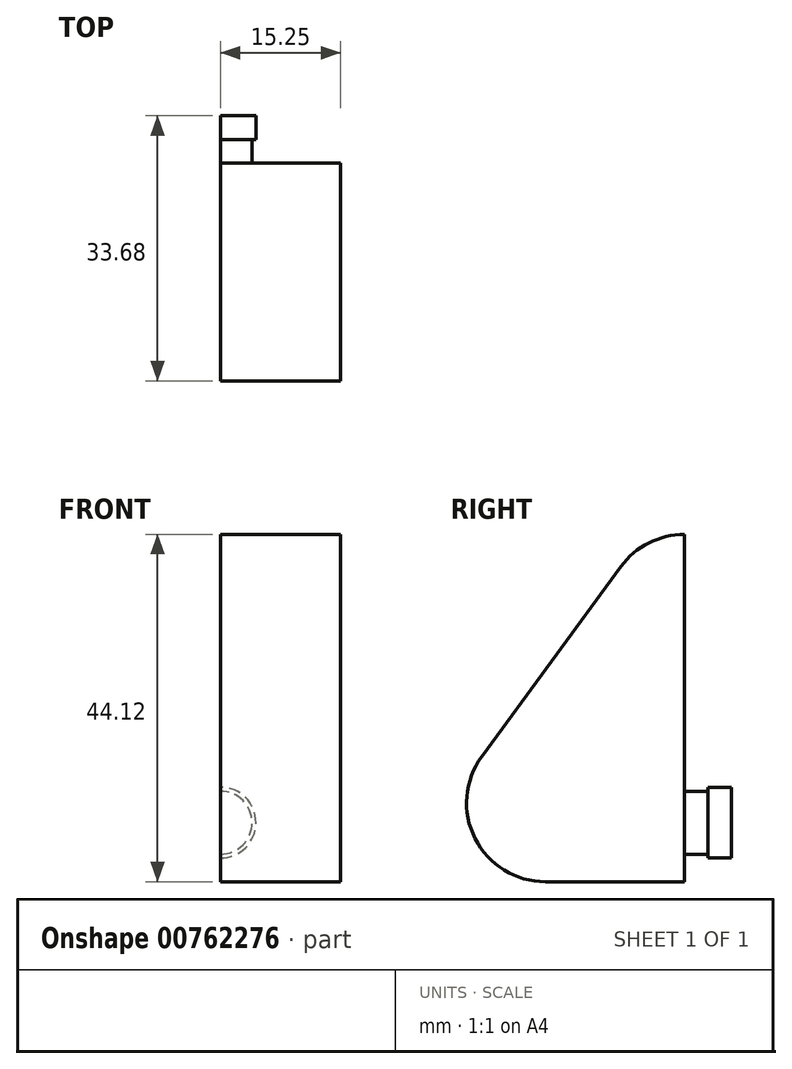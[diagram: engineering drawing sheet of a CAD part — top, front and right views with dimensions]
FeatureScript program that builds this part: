
annotation { "Feature Type Name" : "Feature", "Feature Type Description" : "" }
export const myFeature = defineFeature(function(context is Context, id is Id, definition is map)
    precondition{}
    {
        {
            var Q0;
            Q0=qCreatedBy(makeId("Right.planeOp"),FACE);
            var sketch = newSketch(context, id + "F0", { "sketchPlane" : qUnion([Q0])});
            skLineSegment(sketch, "E0.bottom", {"start": v(27.36, 43.18) * mm, "end": v(-7.64, 43.18) * mm});
            skLineSegment(sketch, "E0.top", {"start": v(27.36, -0.94) * mm, "end": v(-7.64, -0.94) * mm});
            skLineSegment(sketch, "E0.left", {"start": v(27.36, 43.18) * mm, "end": v(27.36, -0.94) * mm});
            skLineSegment(sketch, "E0.right", {"start": v(-7.64, 43.18) * mm, "end": v(-7.64, -0.94) * mm});
            skCircle(sketch, "E1", {"center": v(27.36, 33.18) * mm, "radius": 10 * mm});
            skCircle(sketch, "E2", {"center": v(2.36, -0.94) * mm, "radius": 10 * mm});
            skLineSegment(sketch, "E3", {"start": v(27.36, 33.18) * mm, "end": v(2.36, -0.94) * mm});
            skLineSegment(sketch, "E4", {"start": v(2.36, -0.94) * mm, "end": v(-5.7, 4.97) * mm});
            skLineSegment(sketch, "E5", {"start": v(27.36, 33.18) * mm, "end": v(19.3, 39.1) * mm});
            skLineSegment(sketch, "E6", {"start": v(19.3, 39.1) * mm, "end": v(-5.7, 4.97) * mm});
            skSolve(sketch);
        }
        {
            var Q0;
            {var subQ3=sQuery(id+"F0.wireOp",EDGE,"E5");Q0=makeQuery(id+"F0.imprint","IMPRINT",FACE,{"disambiguationData":[TD([[makeQuery(id+"F0.imprint","IMPRINT",EDGE,{"derivedFrom":subQ3}),-1.0]])]});}
            var Q1;
            {var subQ0=sQuery(id+"F0.wireOp",EDGE,"E5");Q1=makeQuery(id+"F0.imprint","IMPRINT",FACE,{"disambiguationData":[TD([[makeQuery(id+"F0.imprint","IMPRINT",EDGE,{"derivedFrom":subQ0}),1.0]])]});}
            var Q2;
            {var subQ1=sQuery(id+"F0.wireOp",EDGE,"E0.left");var subQ3=sQuery(id+"F0.wireOp",EDGE,"E1");var subQ4=makeQuery(id+"F0.imprint","INTERSECT",VERTEX,{"derivedFrom":[subQ1,subQ3]});Q2=makeQuery(id+"F0.imprint","IMPRINT",FACE,{"disambiguationData":[TD([[makeQuery(id+"F0.imprint","IMPRINT",EDGE,{"disambiguationData":[TD([[subQ4,1.0]])],"derivedFrom":subQ3}),1.0]])]});}
            var Q3;
            {var subQ1=sQuery(id+"F0.wireOp",EDGE,"E0.top");var subQ5=sQuery(id+"F0.wireOp",EDGE,"E0.left");var subQ6=makeQuery(id+"F0.imprint","INTERSECT",VERTEX,{"derivedFrom":[subQ1,subQ5]});Q3=makeQuery(id+"F0.imprint","IMPRINT",FACE,{"disambiguationData":[TD([[makeQuery(id+"F0.imprint","IMPRINT",EDGE,{"disambiguationData":[TD([[subQ6,-1.0]])],"derivedFrom":subQ1}),-1.0]])]});}
            var Q4;
            {var subQ0=sQuery(id+"F0.wireOp",EDGE,"E6");Q4=makeQuery(id+"F0.imprint","IMPRINT",FACE,{"disambiguationData":[TD([[makeQuery(id+"F0.imprint","IMPRINT",EDGE,{"derivedFrom":subQ0}),1.0]])]});}
            var Q5;
            {var subQ0=sQuery(id+"F0.wireOp",EDGE,"E4");Q5=makeQuery(id+"F0.imprint","IMPRINT",FACE,{"disambiguationData":[TD([[makeQuery(id+"F0.imprint","IMPRINT",EDGE,{"derivedFrom":subQ0}),-1.0]])]});}
            var Q6;
            {var subQ3=sQuery(id+"F0.wireOp",EDGE,"E4");Q6=makeQuery(id+"F0.imprint","IMPRINT",FACE,{"disambiguationData":[TD([[makeQuery(id+"F0.imprint","IMPRINT",EDGE,{"derivedFrom":subQ3}),1.0]])]});}
            var Q7;
            {var subQ1=sQuery(id+"F0.wireOp",EDGE,"E0.top");var subQ3=sQuery(id+"F0.wireOp",EDGE,"E2");var subQ4=makeQuery(id+"F0.imprint","INTERSECT",VERTEX,{"derivedFrom":[subQ1,subQ3]});Q7=makeQuery(id+"F0.imprint","IMPRINT",FACE,{"disambiguationData":[TD([[makeQuery(id+"F0.imprint","IMPRINT",EDGE,{"disambiguationData":[TD([[subQ4,-1.0]])],"derivedFrom":subQ3}),1.0]])]});}
            extrude(context, id + "F1", {"entities" : qUnion([Q0, Q1, Q2, Q3, Q4, Q5, Q6, Q7]), "depth" : (13 + 17.5) / 2 * mm, "offsetDistance" : 25 * mm});
        }
        {
            var Q0;
            Q0=makeQuery(id+"F1.opExtrude","SWEPT_EDGE",EDGE,{"disambiguationData":[OSD([sQuery(id+"F0.wireOp",EDGE,"E0.top"),sQuery(id+"F0.wireOp",EDGE,"E0.right"),sQuery(id+"F0.wireOp",EDGE,"E2")])]});
            fillet(context, id + "F2", {"entities" : qUnion([Q0]), "radius" : 10 * mm, "tangentPropagation" : true, "allowEdgeOverflow" : false});
        }
        {
            var Q0;
            Q0=makeQuery(id+"F1.opExtrude","CAP_FACE",FACE,{"disambiguationData":[OSD([sQuery(id+"F0.wireOp",EDGE,"E0.top"),sQuery(id+"F0.wireOp",EDGE,"E0.left"),sQuery(id+"F0.wireOp",EDGE,"E1"),sQuery(id+"F0.wireOp",EDGE,"E2"),sQuery(id+"F0.wireOp",EDGE,"E6")])],"isStart":false});
            var sketch = newSketch(context, id + "F3", { "sketchPlane" : qUnion([Q0])});
            skLineSegment(sketch, "E7.bottom", {"start": v(27.36, 6.56) * mm, "end": v(30.36, 6.56) * mm});
            skLineSegment(sketch, "E7.top", {"start": v(27.36, 2.56) * mm, "end": v(30.36, 2.56) * mm});
            skLineSegment(sketch, "E7.left", {"start": v(27.36, 6.56) * mm, "end": v(27.36, 2.56) * mm});
            skLineSegment(sketch, "E7.right", {"start": v(30.36, 6.56) * mm, "end": v(30.36, 2.56) * mm});
            skLineSegment(sketch, "E8.bottom", {"start": v(30.36, 6.56) * mm, "end": v(33.36, 6.56) * mm});
            skLineSegment(sketch, "E8.top", {"start": v(30.36, 2.06) * mm, "end": v(33.36, 2.06) * mm});
            skLineSegment(sketch, "E8.left", {"start": v(30.36, 6.56) * mm, "end": v(30.36, 2.06) * mm});
            skLineSegment(sketch, "E8.right", {"start": v(33.36, 6.56) * mm, "end": v(33.36, 2.06) * mm});
            skSolve(sketch);
        }
        {
            var Q0;
            {var subQ0=sQuery(id+"F3.wireOp",EDGE,"E7.bottom");Q0=makeQuery(id+"F3.imprint","IMPRINT",FACE,{"disambiguationData":[TD([[makeQuery(id+"F3.imprint","IMPRINT",EDGE,{"derivedFrom":subQ0}),-1.0]])]});}
            var Q1;
            {var subQ3=sQuery(id+"F3.wireOp",EDGE,"E8.bottom");Q1=makeQuery(id+"F3.imprint","IMPRINT",FACE,{"disambiguationData":[TD([[makeQuery(id+"F3.imprint","IMPRINT",EDGE,{"derivedFrom":subQ3}),-1.0]])]});}
            var Q2;
            Q2=sQuery(id+"F3.wireOp",EDGE,"E7.bottom");
            revolve(context, id + "F4", {"operationType" : NewBodyOperationType.ADD, "surfaceOperationType" : NewSurfaceOperationType.NEW, "entities" : qUnion([Q0, Q1]), "axis" : qUnion([Q2]), "revolveType" : RevolveType.ONE_DIRECTION, "angle" : 180 * degree});
        }
        {
            var Q0;
            Q0=makeQuery(id+"F1.opExtrude","SWEPT_BODY",BODY,{"disambiguationData":[OSD([sQuery(id+"F0.wireOp",EDGE,"E0.top"),sQuery(id+"F0.wireOp",EDGE,"E0.left"),sQuery(id+"F0.wireOp",EDGE,"E1"),sQuery(id+"F0.wireOp",EDGE,"E2"),sQuery(id+"F0.wireOp",EDGE,"E6")])]});
            var Q1;
            Q1=makeQuery(id+"F4.boolean.opBoolean","MERGE",FACE,{"derivedFrom":[makeQuery(id+"F1.opExtrude","CAP_FACE",FACE,{"disambiguationData":[OSD([sQuery(id+"F0.wireOp",EDGE,"E0.top"),sQuery(id+"F0.wireOp",EDGE,"E0.left"),sQuery(id+"F0.wireOp",EDGE,"E1"),sQuery(id+"F0.wireOp",EDGE,"E2"),sQuery(id+"F0.wireOp",EDGE,"E6")])],"isStart":false}),makeQuery(id+"F4.opRevolve","CAP_FACE",FACE,{"disambiguationData":[OSD([sQuery(id+"F3.wireOp",EDGE,"E7.bottom"),sQuery(id+"F3.wireOp",EDGE,"E7.top"),sQuery(id+"F3.wireOp",EDGE,"E7.left"),sQuery(id+"F3.wireOp",EDGE,"E8.bottom"),sQuery(id+"F3.wireOp",EDGE,"E8.top"),sQuery(id+"F3.wireOp",EDGE,"E8.left"),sQuery(id+"F3.wireOp",EDGE,"E8.right")])],"isStart":false})]});
            mirror(context, id + "F5", {"entities" : qUnion([Q0]), "mirrorPlane" : qUnion([Q1])});
        }
        {
            var Q0;
            Q0=makeQuery(id+"F1.opExtrude","SWEPT_BODY",BODY,{"disambiguationData":[OSD([sQuery(id+"F0.wireOp",EDGE,"E0.top"),sQuery(id+"F0.wireOp",EDGE,"E0.left"),sQuery(id+"F0.wireOp",EDGE,"E1"),sQuery(id+"F0.wireOp",EDGE,"E2"),sQuery(id+"F0.wireOp",EDGE,"E6")])]});
            deleteBodies(context, id + "F6", {"entities" : qUnion([Q0])});
        }
    });
